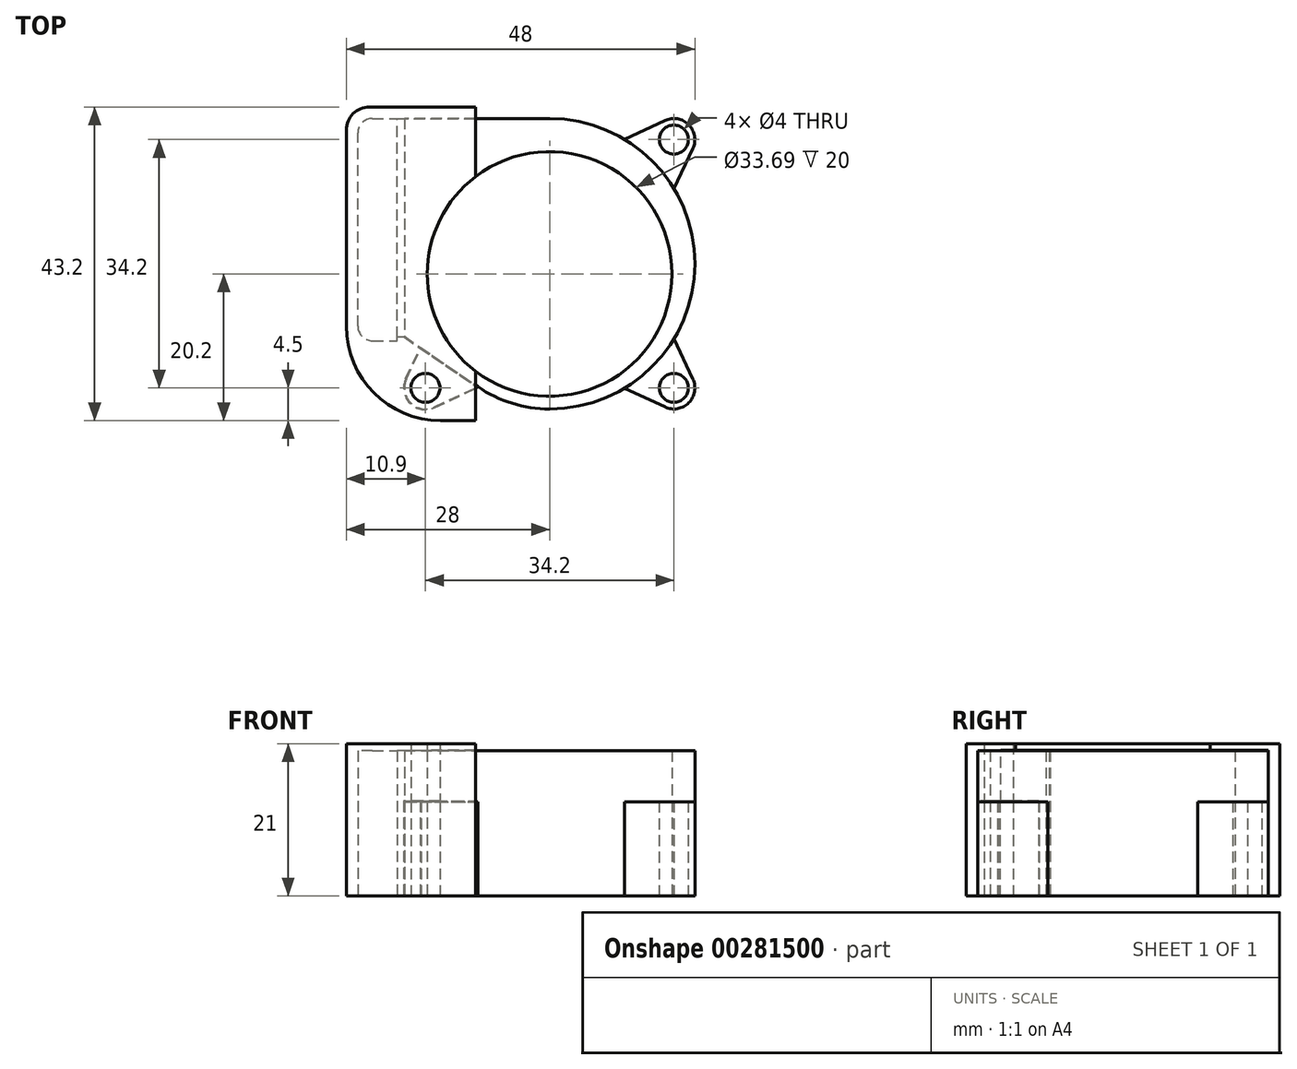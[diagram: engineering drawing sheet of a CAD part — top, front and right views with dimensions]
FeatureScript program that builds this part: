
annotation { "Feature Type Name" : "Feature", "Feature Type Description" : "" }
export const myFeature = defineFeature(function(context is Context, id is Id, definition is map)
    precondition{}
    {
        {
            var Q0;
            Q0=qCreatedBy(makeId("Top.planeOp"),FACE);
            var sketch = newSketch(context, id + "F0", { "sketchPlane" : qUnion([Q0])});
            skCircle(sketch, "E0", {"center": v(0, 0) * mm, "radius": 12.1 * mm, "construction": true});
            skPoint(sketch, "E1", {"position": v(17.1, 18.5) * mm});
            skPoint(sketch, "E2", {"position": v(17.1, -15.7) * mm});
            skPoint(sketch, "E3", {"position": v(-17.1, -15.7) * mm});
            skCircle(sketch, "E4", {"center": v(-17.1, -15.7) * mm, "radius": 2 * mm});
            skCircle(sketch, "E5", {"center": v(17.1, -15.7) * mm, "radius": 2 * mm});
            skCircle(sketch, "E6", {"center": v(17.1, 18.5) * mm, "radius": 2 * mm});
            skCircle(sketch, "E7", {"center": v(-17.1, -15.7) * mm, "radius": 2.9 * mm});
            skCircle(sketch, "E8", {"center": v(17.1, -15.7) * mm, "radius": 2.9 * mm});
            skCircle(sketch, "E9", {"center": v(17.1, 18.5) * mm, "radius": 2.9 * mm});
            skArc(sketch, "E10", {"start": v(19.95, 0) * mm, "mid": v(14.63, 15.04) * mm, "end": v(0, 21.4) * mm});
            skArc(sketch, "E11", {"start": v(0, -18.6) * mm, "mid": v(13.64, -13.23) * mm, "end": v(19.95, 0) * mm});
            skLineSegment(sketch, "E12", {"start": v(15.87, 21.13) * mm, "end": v(10.31, 18.54) * mm});
            skLineSegment(sketch, "E13", {"start": v(19.73, 17.27) * mm, "end": v(17.14, 11.71) * mm});
            skLineSegment(sketch, "E14", {"start": v(19.73, -14.47) * mm, "end": v(17.14, -8.91) * mm});
            skLineSegment(sketch, "E15", {"start": v(15.87, -18.33) * mm, "end": v(10.31, -15.74) * mm});
            skLineSegment(sketch, "E16", {"start": v(17.1, -15.7) * mm, "end": v(-13.85, 15.25) * mm, "construction": true});
            skLineSegment(sketch, "E17", {"start": v(17.1, 18.5) * mm, "end": v(-11.04, -9.64) * mm, "construction": true});
            skLineSegment(sketch, "E18", {"start": v(20, 26.25) * mm, "end": v(20, -32.93) * mm, "construction": true});
            skLineSegment(sketch, "E19", {"start": v(27.8, -18.6) * mm, "end": v(-31.87, -18.6) * mm, "construction": true});
            skLineSegment(sketch, "E20", {"start": v(34.65, 21.4) * mm, "end": v(-24.29, 21.4) * mm, "construction": true});
            skLineSegment(sketch, "E21", {"start": v(-20, -24.96) * mm, "end": v(-20, 29.24) * mm, "construction": true});
            skLineSegment(sketch, "E22", {"start": v(0, 21.4) * mm, "end": v(-20, 21.4) * mm});
            skLineSegment(sketch, "E23", {"start": v(-20, 21.4) * mm, "end": v(-20, -8.6) * mm});
            skLineSegment(sketch, "E24", {"start": v(-20, -8.6) * mm, "end": v(-9.89, -15.54) * mm});
            skArc(sketch, "E25", {"start": v(-9.89, -15.54) * mm, "mid": v(-5.18, -17.82) * mm, "end": v(0, -18.6) * mm});
            skLineSegment(sketch, "E26", {"start": v(-17.1, -15.7) * mm, "end": v(-5.62, -4.22) * mm, "construction": true});
            skLineSegment(sketch, "E27", {"start": v(-19.73, -14.47) * mm, "end": v(-17.72, -10.16) * mm});
            skLineSegment(sketch, "E28", {"start": v(-15.87, -18.33) * mm, "end": v(-9.89, -15.54) * mm});
            skSolve(sketch);
        }
        {
            var Q0;
            {var subQ8=sQuery(id+"F0.wireOp",EDGE,"E22");Q0=makeQuery(id+"F0.imprint","IMPRINT",FACE,{"disambiguationData":[TD([[makeQuery(id+"F0.imprint","IMPRINT",EDGE,{"derivedFrom":subQ8}),1.0]])]});}
            extrude(context, id + "F1", {"entities" : qUnion([Q0]), "depth" : 20 * mm});
        }
        {
            var Q0;
            {var subQ0=sQuery(id+"F0.wireOp",EDGE,"E27");Q0=makeQuery(id+"F0.imprint","IMPRINT",FACE,{"disambiguationData":[TD([[makeQuery(id+"F0.imprint","IMPRINT",EDGE,{"derivedFrom":subQ0}),-1.0]])]});}
            var Q1;
            Q1=makeQuery(id+"F0.imprint","IMPRINT",FACE,{"disambiguationData":[TD([[makeQuery(id+"F0.imprint","IMPRINT",EDGE,{"derivedFrom":sQuery(id+"F0.wireOp",EDGE,"E4")}),-1.0]])]});
            var Q2;
            {var subQ0=sQuery(id+"F0.wireOp",EDGE,"E14");Q2=makeQuery(id+"F0.imprint","IMPRINT",FACE,{"disambiguationData":[TD([[makeQuery(id+"F0.imprint","IMPRINT",EDGE,{"derivedFrom":subQ0}),1.0]])]});}
            var Q3;
            Q3=makeQuery(id+"F0.imprint","IMPRINT",FACE,{"disambiguationData":[TD([[makeQuery(id+"F0.imprint","IMPRINT",EDGE,{"derivedFrom":sQuery(id+"F0.wireOp",EDGE,"E5")}),-1.0]])]});
            var Q4;
            {var subQ0=sQuery(id+"F0.wireOp",EDGE,"E12");Q4=makeQuery(id+"F0.imprint","IMPRINT",FACE,{"disambiguationData":[TD([[makeQuery(id+"F0.imprint","IMPRINT",EDGE,{"derivedFrom":subQ0}),1.0]])]});}
            var Q5;
            Q5=makeQuery(id+"F0.imprint","IMPRINT",FACE,{"disambiguationData":[TD([[makeQuery(id+"F0.imprint","IMPRINT",EDGE,{"derivedFrom":sQuery(id+"F0.wireOp",EDGE,"E6")}),-1.0]])]});
            extrude(context, id + "F2", {"entities" : qUnion([Q0, Q1, Q2, Q3, Q4, Q5]), "operationType" : NewBodyOperationType.ADD, "depth" : 13 * mm});
        }
        {
            var Q0;
            Q0=qCreatedBy(makeId("Top.planeOp"),FACE);
            var sketch = newSketch(context, id + "F3", { "sketchPlane" : qUnion([Q0])});
            skLineSegment(sketch, "E29.bottom", {"start": v(-28, 23) * mm, "end": v(-10.2, 23) * mm});
            skLineSegment(sketch, "E29.top", {"start": v(-28, -20.2) * mm, "end": v(-10.2, -20.2) * mm});
            skLineSegment(sketch, "E29.left", {"start": v(-28, 23) * mm, "end": v(-28, -20.2) * mm});
            skLineSegment(sketch, "E29.right", {"start": v(-10.2, 23) * mm, "end": v(-10.2, -20.2) * mm});
            skSolve(sketch);
        }
        {
            var Q0;
            Q0=makeQuery(id+"F3.imprint","IMPRINT",FACE,{"disambiguationData":[TD([[makeQuery(id+"F3.imprint","IMPRINT",EDGE,{"derivedFrom":sQuery(id+"F3.wireOp",EDGE,"E29.bottom")}),-1.0]])]});
            extrude(context, id + "F4", {"entities" : qUnion([Q0]), "depth" : 21 * mm, "hasSecondDirection" : true, "secondDirectionOppositeDirection" : true, "secondDirectionDepth" : 1 * mm});
        }
        {
            var Q0;
            Q0=makeQuery(id+"F4.opExtrude","CAP_FACE",FACE,{"disambiguationData":[OSD([sQuery(id+"F3.wireOp",EDGE,"E29.bottom"),sQuery(id+"F3.wireOp",EDGE,"E29.top"),sQuery(id+"F3.wireOp",EDGE,"E29.left"),sQuery(id+"F3.wireOp",EDGE,"E29.right")])],"isStart":true});
            var sketch = newSketch(context, id + "F5", { "sketchPlane" : qUnion([Q0])});
            skLineSegment(sketch, "E30.bottom", {"start": v(-26.4, 9.2) * mm, "end": v(-21, 9.2) * mm});
            skLineSegment(sketch, "E30.top", {"start": v(-26.4, -21.4) * mm, "end": v(-21, -21.4) * mm});
            skLineSegment(sketch, "E30.left", {"start": v(-26.4, 9.2) * mm, "end": v(-26.4, -21.4) * mm});
            skLineSegment(sketch, "E30.right", {"start": v(-21, 9.2) * mm, "end": v(-21, -21.4) * mm});
            skSolve(sketch);
        }
        {
            var Q0;
            Q0=makeQuery(id+"F5.imprint","IMPRINT",FACE,{"disambiguationData":[TD([[makeQuery(id+"F5.imprint","IMPRINT",EDGE,{"derivedFrom":sQuery(id+"F5.wireOp",EDGE,"E30.bottom")}),-1.0]])]});
            extrude(context, id + "F6", {"entities" : qUnion([Q0]), "operationType" : NewBodyOperationType.REMOVE, "oppositeDirection" : true, "depth" : 21 * mm});
        }
        {
            var Q0;
            Q0=makeQuery(id+"F1.opExtrude","SWEPT_BODY",BODY,{"disambiguationData":[OSD([sQuery(id+"F0.wireOp",EDGE,"E10"),sQuery(id+"F0.wireOp",EDGE,"E11"),sQuery(id+"F0.wireOp",EDGE,"E22"),sQuery(id+"F0.wireOp",EDGE,"E23"),sQuery(id+"F0.wireOp",EDGE,"E24"),sQuery(id+"F0.wireOp",EDGE,"E25")])]});
            var Q1;
            Q1=makeQuery(id+"F4.opExtrude","SWEPT_BODY",BODY,{"disambiguationData":[OSD([sQuery(id+"F3.wireOp",EDGE,"E29.bottom"),sQuery(id+"F3.wireOp",EDGE,"E29.top"),sQuery(id+"F3.wireOp",EDGE,"E29.left"),sQuery(id+"F3.wireOp",EDGE,"E29.right")])]});
            var Q2;
            Q2=makeQuery(id+"F1.opExtrude","SWEPT_FACE",FACE,{"disambiguationData":[OSD([sQuery(id+"F0.wireOp",EDGE,"E22")])]});
            var Q3;
            Q3=makeQuery(id+"F2.opExtrude","SWEPT_FACE",FACE,{"disambiguationData":[OSD([sQuery(id+"F0.wireOp",EDGE,"E28")])]});
            var Q4;
            Q4=makeQuery(id+"F2.opExtrude","SWEPT_FACE",FACE,{"disambiguationData":[OSD([sQuery(id+"F0.wireOp",EDGE,"E7")])]});
            var Q5;
            Q5=makeQuery(id+"F2.opExtrude","SWEPT_FACE",FACE,{"disambiguationData":[OSD([sQuery(id+"F0.wireOp",EDGE,"E27")])]});
            var Q6;
            Q6=makeQuery(id+"F1.opExtrude","SWEPT_FACE",FACE,{"disambiguationData":[OSD([sQuery(id+"F0.wireOp",EDGE,"E24")])]});
            var Q7;
            {var subQ0=sQuery(id+"F0.wireOp",EDGE,"E10");var subQ1=sQuery(id+"F0.wireOp",EDGE,"E11");var subQ2=sQuery(id+"F0.wireOp",EDGE,"E24");Q7=makeQuery(id+"F2.boolean.opBoolean","MERGE",FACE,{"derivedFrom":[makeQuery(id+"F1.opExtrude","CAP_FACE",FACE,{"disambiguationData":[OSD([subQ0,subQ1,sQuery(id+"F0.wireOp",EDGE,"E22"),sQuery(id+"F0.wireOp",EDGE,"E23"),subQ2,sQuery(id+"F0.wireOp",EDGE,"E25")])],"isStart":true}),makeQuery(id+"F2.opExtrude","CAP_FACE",FACE,{"disambiguationData":[OSD([sQuery(id+"F0.wireOp",EDGE,"E4"),sQuery(id+"F0.wireOp",EDGE,"E7"),subQ2,sQuery(id+"F0.wireOp",EDGE,"E27"),sQuery(id+"F0.wireOp",EDGE,"E28")])],"isStart":true}),makeQuery(id+"F2.opExtrude","CAP_FACE",FACE,{"disambiguationData":[OSD([sQuery(id+"F0.wireOp",EDGE,"E5"),sQuery(id+"F0.wireOp",EDGE,"E8"),subQ1,sQuery(id+"F0.wireOp",EDGE,"E14"),sQuery(id+"F0.wireOp",EDGE,"E15")])],"isStart":true}),makeQuery(id+"F2.opExtrude","CAP_FACE",FACE,{"disambiguationData":[OSD([sQuery(id+"F0.wireOp",EDGE,"E6"),sQuery(id+"F0.wireOp",EDGE,"E9"),subQ0,sQuery(id+"F0.wireOp",EDGE,"E12"),sQuery(id+"F0.wireOp",EDGE,"E13")])],"isStart":true})]});}
            var Q8;
            Q8=makeQuery(id+"F2.opExtrude","CAP_FACE",FACE,{"disambiguationData":[OSD([sQuery(id+"F0.wireOp",EDGE,"E4"),sQuery(id+"F0.wireOp",EDGE,"E7"),sQuery(id+"F0.wireOp",EDGE,"E24"),sQuery(id+"F0.wireOp",EDGE,"E27"),sQuery(id+"F0.wireOp",EDGE,"E28")])],"isStart":false});
            var Q9;
            Q9=makeQuery(id+"F2.opExtrude","SWEPT_FACE",FACE,{"disambiguationData":[OSD([sQuery(id+"F0.wireOp",EDGE,"E4")])]});
            var Q10;
            Q10=makeQuery(id+"F1.opExtrude","SWEPT_FACE",FACE,{"disambiguationData":[OSD([sQuery(id+"F0.wireOp",EDGE,"E25")])]});
            var Q11;
            Q11=makeQuery(id+"F1.opExtrude","CAP_FACE",FACE,{"disambiguationData":[OSD([sQuery(id+"F0.wireOp",EDGE,"E10"),sQuery(id+"F0.wireOp",EDGE,"E11"),sQuery(id+"F0.wireOp",EDGE,"E22"),sQuery(id+"F0.wireOp",EDGE,"E23"),sQuery(id+"F0.wireOp",EDGE,"E24"),sQuery(id+"F0.wireOp",EDGE,"E25")])],"isStart":false});
            booleanBodies(context, id + "F7", {"operationType" : BooleanOperationType.SUBTRACTION, "tools" : qUnion([Q0]), "targets" : qUnion([Q1]), "offset" : true, "entitiesToOffset" : qUnion([Q2, Q3, Q4, Q5, Q6, Q7, Q8, Q9, Q10, Q11]), "offsetDistance" : .1 * mm, "keepTools" : true});
        }
        {
            var Q0;
            Q0=sQuery(id+"F0.wireOp",VERTEX,"E3");
            var Q1;
            Q1=makeQuery(id+"F4.opExtrude","SWEPT_BODY",BODY,{"disambiguationData":[OSD([sQuery(id+"F3.wireOp",EDGE,"E29.bottom"),sQuery(id+"F3.wireOp",EDGE,"E29.top"),sQuery(id+"F3.wireOp",EDGE,"E29.left"),sQuery(id+"F3.wireOp",EDGE,"E29.right")])]});
            hole(context, id + "F8", {"style" : HoleStyle.SIMPLE, "endStyle" : HoleEndStyle.THROUGH, "oppositeDirection" : true, "holeDiameter" : 4 * mm, "tappedDepth" : 20 * mm, "tapClearance" : 0, "startFromSketch" : true, "locations" : qUnion([Q0]), "scope" : qUnion([Q1])});
        }
        {
            var Q0;
            Q0=makeQuery(id+"F7.tempBoolean.opBoolean","COPY",FACE,{"derivedFrom":makeQuery(id+"F7.offsetTempBody.opPattern","COPY",FACE,{"derivedFrom":makeQuery(id+"F1.opExtrude","SWEPT_FACE",FACE,{"disambiguationData":[OSD([sQuery(id+"F0.wireOp",EDGE,"E23")])]}),"instanceName":"1"})});
            extrude(context, id + "F9", {"entities" : qUnion([Q0]), "operationType" : NewBodyOperationType.REMOVE, "oppositeDirection" : true, "depth" : 1 * mm});
        }
        {
            var Q0;
            Q0=makeQuery(id+"F6.boolean.opBoolean","COPY",EDGE,{"derivedFrom":makeQuery(id+"F6.opExtrude","SWEPT_EDGE",EDGE,{"disambiguationData":[OSD([sQuery(id+"F5.wireOp",EDGE,"E30.top"),sQuery(id+"F5.wireOp",EDGE,"E30.left")])]})});
            var Q1;
            Q1=makeQuery(id+"F6.boolean.opBoolean","COPY",EDGE,{"derivedFrom":makeQuery(id+"F6.opExtrude","SWEPT_EDGE",EDGE,{"disambiguationData":[OSD([sQuery(id+"F5.wireOp",EDGE,"E30.bottom"),sQuery(id+"F5.wireOp",EDGE,"E30.left")])]})});
            fillet(context, id + "F10", {"entities" : qUnion([Q0, Q1]), "radius" : 2 * mm, "tangentPropagation" : true, "allowEdgeOverflow" : false});
        }
        {
            var Q0;
            Q0=makeQuery(id+"F4.opExtrude","SWEPT_EDGE",EDGE,{"disambiguationData":[OSD([sQuery(id+"F3.wireOp",EDGE,"E29.bottom"),sQuery(id+"F3.wireOp",EDGE,"E29.left")])]});
            fillet(context, id + "F11", {"entities" : qUnion([Q0]), "radius" : 3.2 * mm, "tangentPropagation" : true, "allowEdgeOverflow" : false});
        }
        {
            var Q0;
            Q0=makeQuery(id+"F4.opExtrude","SWEPT_EDGE",EDGE,{"disambiguationData":[OSD([sQuery(id+"F3.wireOp",EDGE,"E29.top"),sQuery(id+"F3.wireOp",EDGE,"E29.left")])]});
            fillet(context, id + "F12", {"entities" : qUnion([Q0]), "radius" : 13 * mm, "tangentPropagation" : true, "allowEdgeOverflow" : false});
        }
        {
            var Q0;
            Q0=makeQuery(id+"F4.opExtrude","CAP_FACE",FACE,{"disambiguationData":[OSD([sQuery(id+"F3.wireOp",EDGE,"E29.bottom"),sQuery(id+"F3.wireOp",EDGE,"E29.top"),sQuery(id+"F3.wireOp",EDGE,"E29.left"),sQuery(id+"F3.wireOp",EDGE,"E29.right")])],"isStart":true});
            extrude(context, id + "F13", {"entities" : qUnion([Q0]), "operationType" : NewBodyOperationType.REMOVE, "oppositeDirection" : true, "depth" : 1 * mm});
        }
        {
            var Q0;
            Q0=qCreatedBy(makeId("Top.planeOp"),FACE);
            var sketch = newSketch(context, id + "F14", { "sketchPlane" : qUnion([Q0])});
            skCircle(sketch, "E31", {"center": v(0, 0) * mm, "radius": 16.85 * mm});
            skSolve(sketch);
        }
        {
            var Q0;
            Q0 = qSketchRegion(id + "F14", true);
            extrude(context, id + "F15", {"entities" : qUnion([Q0]), "operationType" : NewBodyOperationType.REMOVE, "depth" : 25 * mm});
        }
        {
            var Q0;
            {var subQ0=sQuery(id+"F0.wireOp",EDGE,"E22");Q0=makeQuery(id+"F9.boolean.opBoolean","MERGE",FACE,{"derivedFrom":[makeQuery(id+"F7.tempBoolean.opBoolean","COPY",FACE,{"derivedFrom":makeQuery(id+"F7.offsetTempBody.opPattern","COPY",FACE,{"derivedFrom":makeQuery(id+"F1.opExtrude","SWEPT_FACE",FACE,{"disambiguationData":[OSD([subQ0])]}),"instanceName":"1"})}),makeQuery(id+"F9.opExtrude","SWEPT_FACE",FACE,{"disambiguationData":[OSD([subQ0,sQuery(id+"F0.wireOp",EDGE,"E23")])]})]});}
            var Q1;
            Q1=makeQuery(id+"F6.boolean.opBoolean","COPY",FACE,{"derivedFrom":makeQuery(id+"F6.opExtrude","SWEPT_FACE",FACE,{"disambiguationData":[OSD([sQuery(id+"F5.wireOp",EDGE,"E30.top")])]})});
            extrude(context, id + "F16", {"entities" : qUnion([Q0]), "operationType" : NewBodyOperationType.ADD, "endBound" : BoundingType.UP_TO_SURFACE, "endBoundEntityFace" : qUnion([Q1]), "depth" : 25 * mm});
        }
    });
